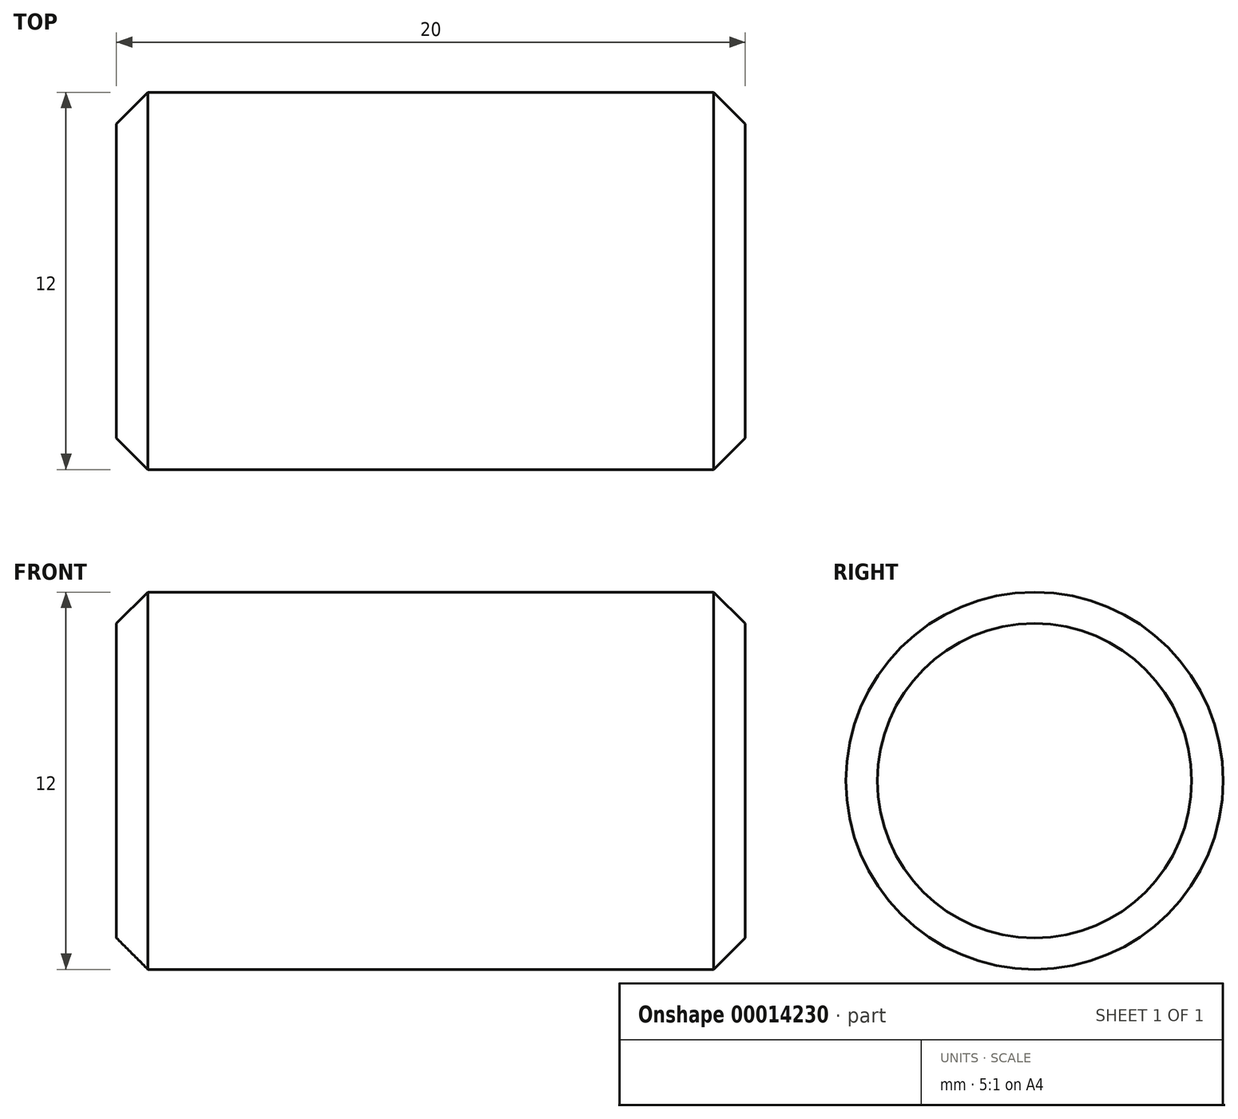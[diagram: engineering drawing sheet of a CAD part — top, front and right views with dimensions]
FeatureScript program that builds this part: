
annotation { "Feature Type Name" : "Feature", "Feature Type Description" : "" }
export const myFeature = defineFeature(function(context is Context, id is Id, definition is map)
    precondition{}
    {
        {
            var Q0;
            Q0=qCreatedBy(makeId("Right.planeOp"),FACE);
            var sketch = newSketch(context, id + "F0", { "sketchPlane" : qUnion([Q0])});
            skCircle(sketch, "E0", {"center": v(0, 0) * mm, "radius": 6 * mm});
            skSolve(sketch);
        }
        {
            var Q0;
            Q0=qSketchRegion(id+"F0",true);
            extrude(context, id + "F1", {"entities" : qUnion([Q0]), "depth" : 20 * mm});
        }
        {
            var Q0;
            Q0=makeQuery(id+"F1.opExtrude","CAP_EDGE",EDGE,{"disambiguationData":[OSD([sQuery(id+"F0.wireOp",EDGE,"E0")])],"isStart":false});
            var Q1;
            Q1=makeQuery(id+"F1.opExtrude","CAP_EDGE",EDGE,{"disambiguationData":[OSD([sQuery(id+"F0.wireOp",EDGE,"E0")])],"isStart":true});
            chamfer(context, id + "F2", {"entities" : qUnion([Q0, Q1]), "width" : 1 * mm, "tangentPropagation" : true});
        }
    });
